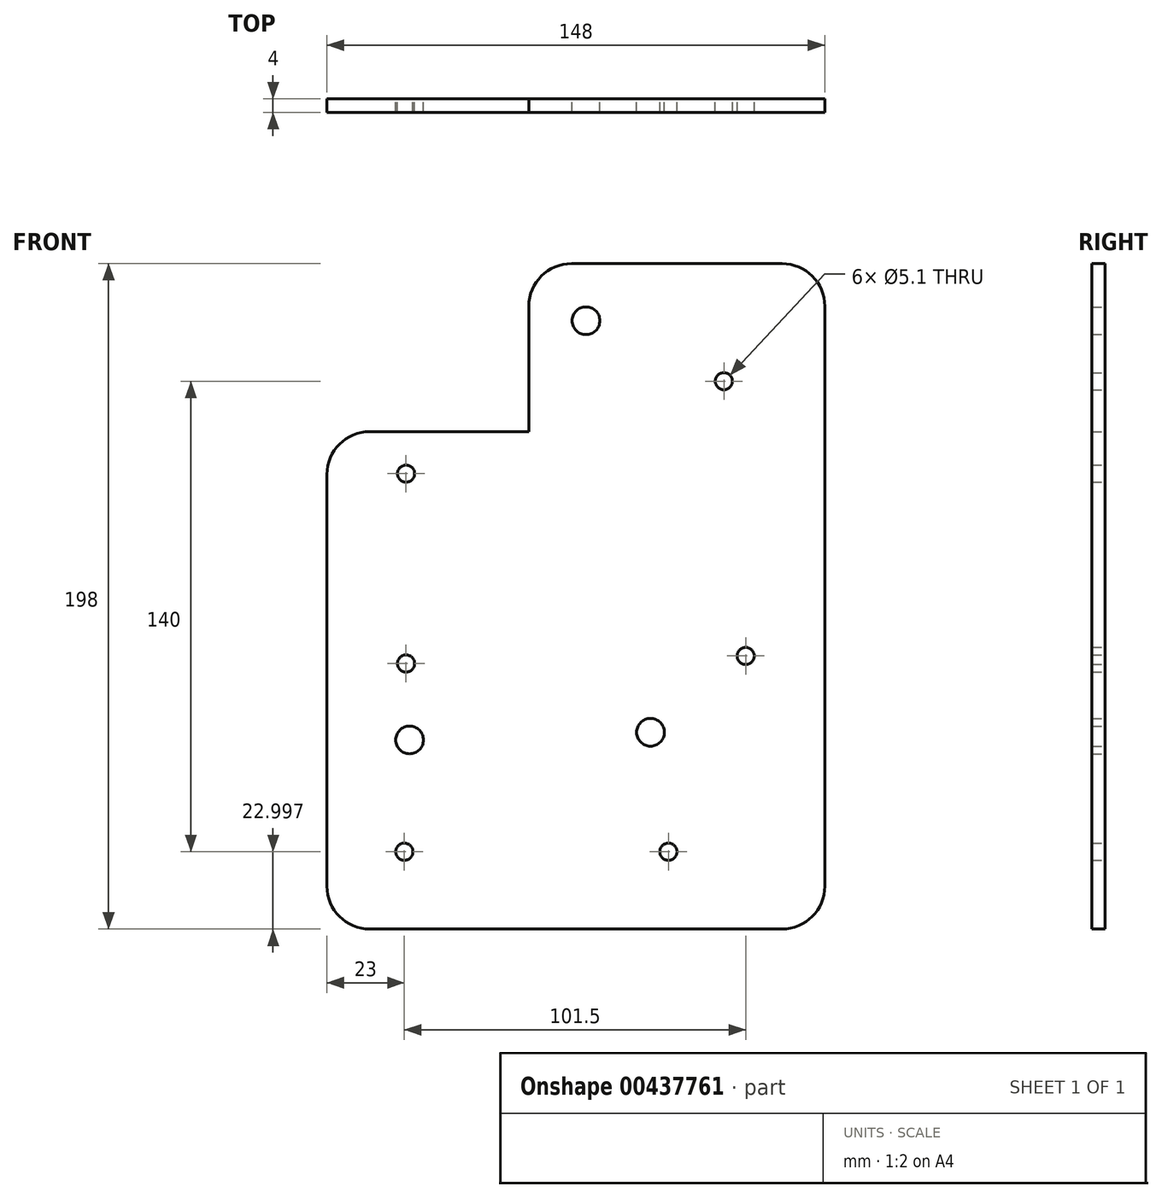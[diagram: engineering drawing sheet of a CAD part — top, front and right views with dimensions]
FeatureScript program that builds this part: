
annotation { "Feature Type Name" : "Feature", "Feature Type Description" : "" }
export const myFeature = defineFeature(function(context is Context, id is Id, definition is map)
    precondition{}
    {
        {
            var Q0;
            Q0=qCreatedBy(makeId("Front.planeOp"),FACE);
            var sketch = newSketch(context, id + "F0", { "sketchPlane" : qUnion([Q0])});
            skPoint(sketch, "E0", {"position": v(0, 84.1) * mm});
            skPoint(sketch, "E1.MirrorP", {"position": v(19.18, -38.37) * mm});
            skPoint(sketch, "E2.MirrorP", {"position": v(-52.45, -40.65) * mm});
            skCircle(sketch, "E3", {"center": v(-52.45, -40.65) * mm, "radius": 4.12 * mm});
            skCircle(sketch, "E4", {"center": v(19.18, -38.37) * mm, "radius": 4.12 * mm});
            skCircle(sketch, "E5", {"center": v(0, 84.1) * mm, "radius": 4.12 * mm});
            skSolve(sketch);
        }
        {
            var Q0;
            Q0=qCreatedBy(makeId("Front.planeOp"),FACE);
            var sketch = newSketch(context, id + "F1", { "sketchPlane" : qUnion([Q0])});
            skLineSegment(sketch, "E6", {"start": v(-17, 88.4) * mm, "end": v(-17, 51.1) * mm});
            skLineSegment(sketch, "E7", {"start": v(-4.3, 101.1) * mm, "end": v(58.3, 101.1) * mm});
            skLineSegment(sketch, "E8", {"start": v(-17, 51.1) * mm, "end": v(-64.3, 51.1) * mm});
            skLineSegment(sketch, "E9", {"start": v(-77, 38.4) * mm, "end": v(-77, -84.2) * mm});
            skLineSegment(sketch, "E10", {"start": v(-64.3, -96.9) * mm, "end": v(58.3, -96.9) * mm});
            skLineSegment(sketch, "E11", {"start": v(71, -84.2) * mm, "end": v(71, 88.4) * mm});
            skPoint(sketch, "E12.visualSharp", {"position": v(-17, 101.1) * mm});
            skArc(sketch, "E12.filletArc", {"start": v(-4.3, 101.1) * mm, "mid": v(-13.28, 97.38) * mm, "end": v(-17, 88.4) * mm});
            skPoint(sketch, "E13.visualSharp", {"position": v(71, 101.1) * mm});
            skArc(sketch, "E13.filletArc", {"start": v(71, 88.4) * mm, "mid": v(67.28, 97.38) * mm, "end": v(58.3, 101.1) * mm});
            skPoint(sketch, "E14.visualSharp", {"position": v(71, -96.9) * mm});
            skArc(sketch, "E14.filletArc", {"start": v(58.3, -96.9) * mm, "mid": v(67.28, -93.18) * mm, "end": v(71, -84.2) * mm});
            skPoint(sketch, "E15.visualSharp", {"position": v(-77, -96.9) * mm});
            skArc(sketch, "E15.filletArc", {"start": v(-77, -84.2) * mm, "mid": v(-73.28, -93.18) * mm, "end": v(-64.3, -96.9) * mm});
            skPoint(sketch, "E16.visualSharp", {"position": v(-77, 51.1) * mm});
            skArc(sketch, "E16.filletArc", {"start": v(-64.3, 51.1) * mm, "mid": v(-73.28, 47.38) * mm, "end": v(-77, 38.4) * mm});
            skSolve(sketch);
        }
        {
            var Q0;
            Q0=qCreatedBy(makeId("Front.planeOp"),FACE);
            var sketch = newSketch(context, id + "F2", { "sketchPlane" : qUnion([Q0])});
            skCircle(sketch, "E17", {"center": v(-53.5, 38.6) * mm, "radius": 2.55 * mm});
            skCircle(sketch, "E18", {"center": v(-53.5, -17.9) * mm, "radius": 2.55 * mm});
            skSolve(sketch);
        }
        {
            var Q0;
            Q0=qCreatedBy(makeId("Front.planeOp"),FACE);
            var sketch = newSketch(context, id + "F3", { "sketchPlane" : qUnion([Q0])});
            skCircle(sketch, "E19", {"center": v(41, 66.1) * mm, "radius": 2.55 * mm});
            skCircle(sketch, "E20", {"center": v(47.5, -15.65) * mm, "radius": 2.55 * mm});
            skSolve(sketch);
        }
        {
            var Q0;
            Q0=qCreatedBy(makeId("Front.planeOp"),FACE);
            var sketch = newSketch(context, id + "F4", { "sketchPlane" : qUnion([Q0])});
            skCircle(sketch, "E21", {"center": v(-54, -73.9) * mm, "radius": 2.55 * mm});
            skCircle(sketch, "E22", {"center": v(24.5, -73.9) * mm, "radius": 2.55 * mm});
            skSolve(sketch);
        }
        {
            var Q0;
            Q0 = qSketchRegion(id + "F1", true);
            extrude(context, id + "F5", {"entities" : qUnion([Q0]), "depth" : 4 * mm, "offsetDistance" : 25.4 * mm});
        }
        {
            var Q0;
            Q0 = qSketchRegion(id + "F0", true);
            extrude(context, id + "F6", {"entities" : qUnion([Q0]), "operationType" : NewBodyOperationType.REMOVE, "depth" : 32 * mm, "offsetDistance" : 25.4 * mm});
        }
        {
            var Q0;
            Q0 = qSketchRegion(id + "F4", true);
            extrude(context, id + "F7", {"entities" : qUnion([Q0]), "operationType" : NewBodyOperationType.REMOVE, "depth" : 18.54 * mm, "offsetDistance" : 25.4 * mm});
        }
        {
            var Q0;
            Q0 = qSketchRegion(id + "F2", true);
            extrude(context, id + "F8", {"entities" : qUnion([Q0]), "operationType" : NewBodyOperationType.REMOVE, "depth" : 16.76 * mm, "offsetDistance" : 25.4 * mm});
        }
        {
            var Q0;
            Q0 = qSketchRegion(id + "F3", true);
            extrude(context, id + "F9", {"entities" : qUnion([Q0]), "operationType" : NewBodyOperationType.REMOVE, "depth" : 10.67 * mm, "offsetDistance" : 25.4 * mm});
        }
    });
